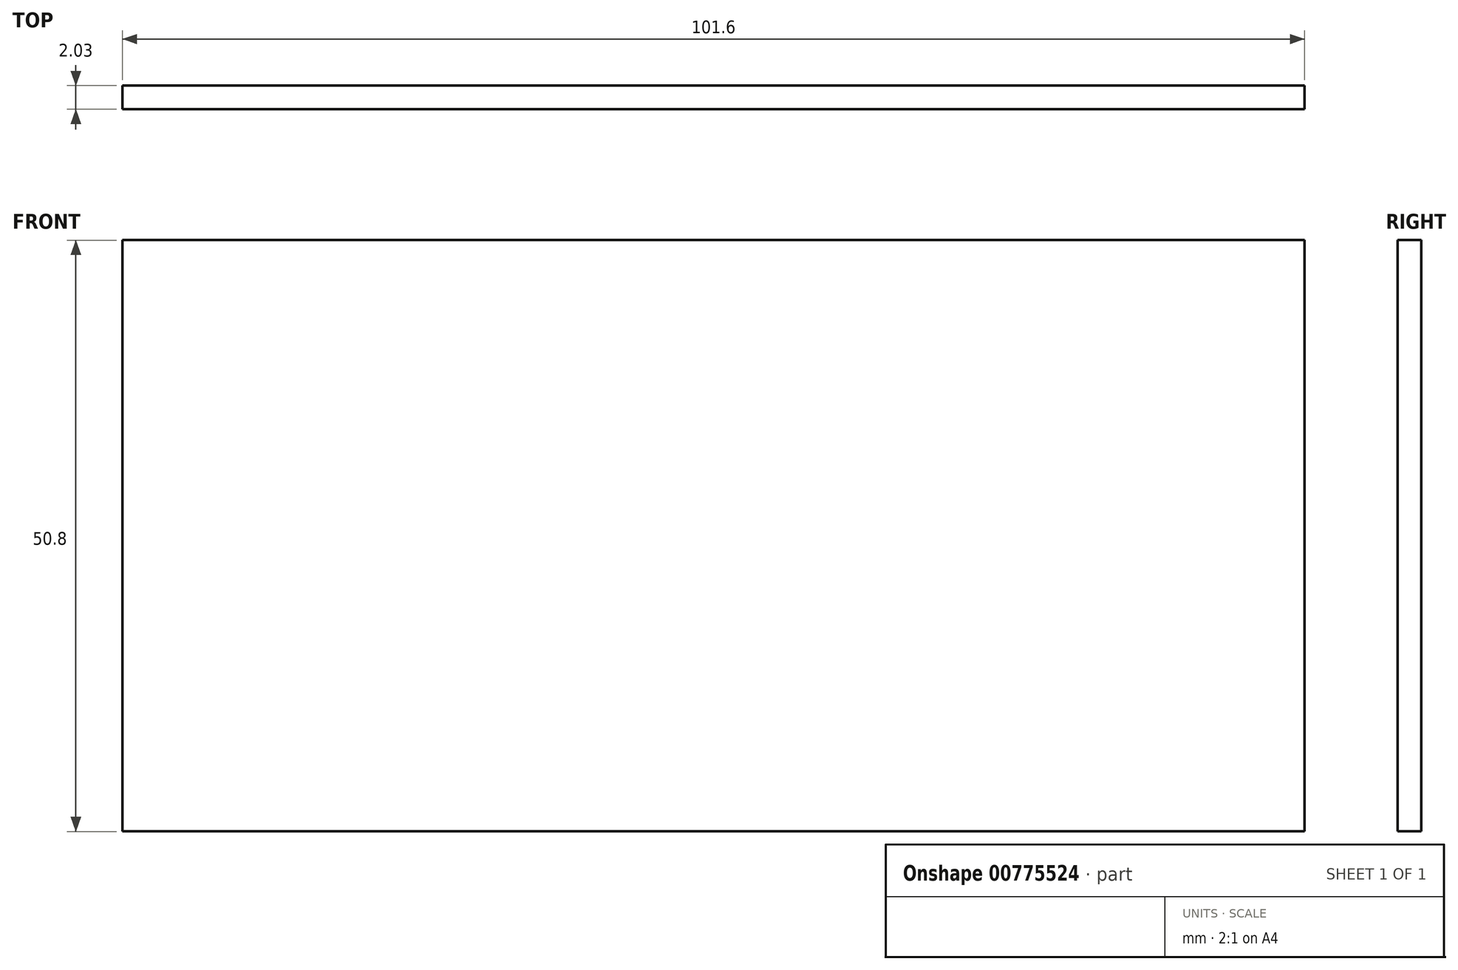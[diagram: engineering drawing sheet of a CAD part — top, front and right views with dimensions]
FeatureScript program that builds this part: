
annotation { "Feature Type Name" : "Feature", "Feature Type Description" : "" }
export const myFeature = defineFeature(function(context is Context, id is Id, definition is map)
    precondition{}
    {
        {
            var Q0;
            Q0=qCreatedBy(makeId("Front.planeOp"),FACE);
            var sketch = newSketch(context, id + "F0", { "sketchPlane" : qUnion([Q0])});
            skLineSegment(sketch, "E0", {"start": v(0, 0) * mm, "end": v(0, 60.65) * mm, "construction": true});
            skLineSegment(sketch, "E1.bottom", {"start": v(53.76, 24.65) * mm, "end": v(-47.84, 24.65) * mm});
            skLineSegment(sketch, "E1.top", {"start": v(53.76, -26.15) * mm, "end": v(-47.84, -26.15) * mm});
            skLineSegment(sketch, "E1.left", {"start": v(53.76, 24.65) * mm, "end": v(53.76, -26.15) * mm});
            skLineSegment(sketch, "E1.right", {"start": v(-47.84, 24.65) * mm, "end": v(-47.84, -26.15) * mm});
            skSolve(sketch);
        }
        {
            var Q0;
            Q0=makeQuery(id+"F0.imprint","IMPRINT",FACE,{"disambiguationData":[TD([[makeQuery(id+"F0.imprint","IMPRINT",EDGE,{"derivedFrom":sQuery(id+"F0.wireOp",EDGE,"E1.bottom")}),1.0]])]});
            extrude(context, id + "F1", {"entities" : qUnion([Q0]), "depth" : 2.03 * mm, "offsetDistance" : 25.4 * mm});
        }
    });
